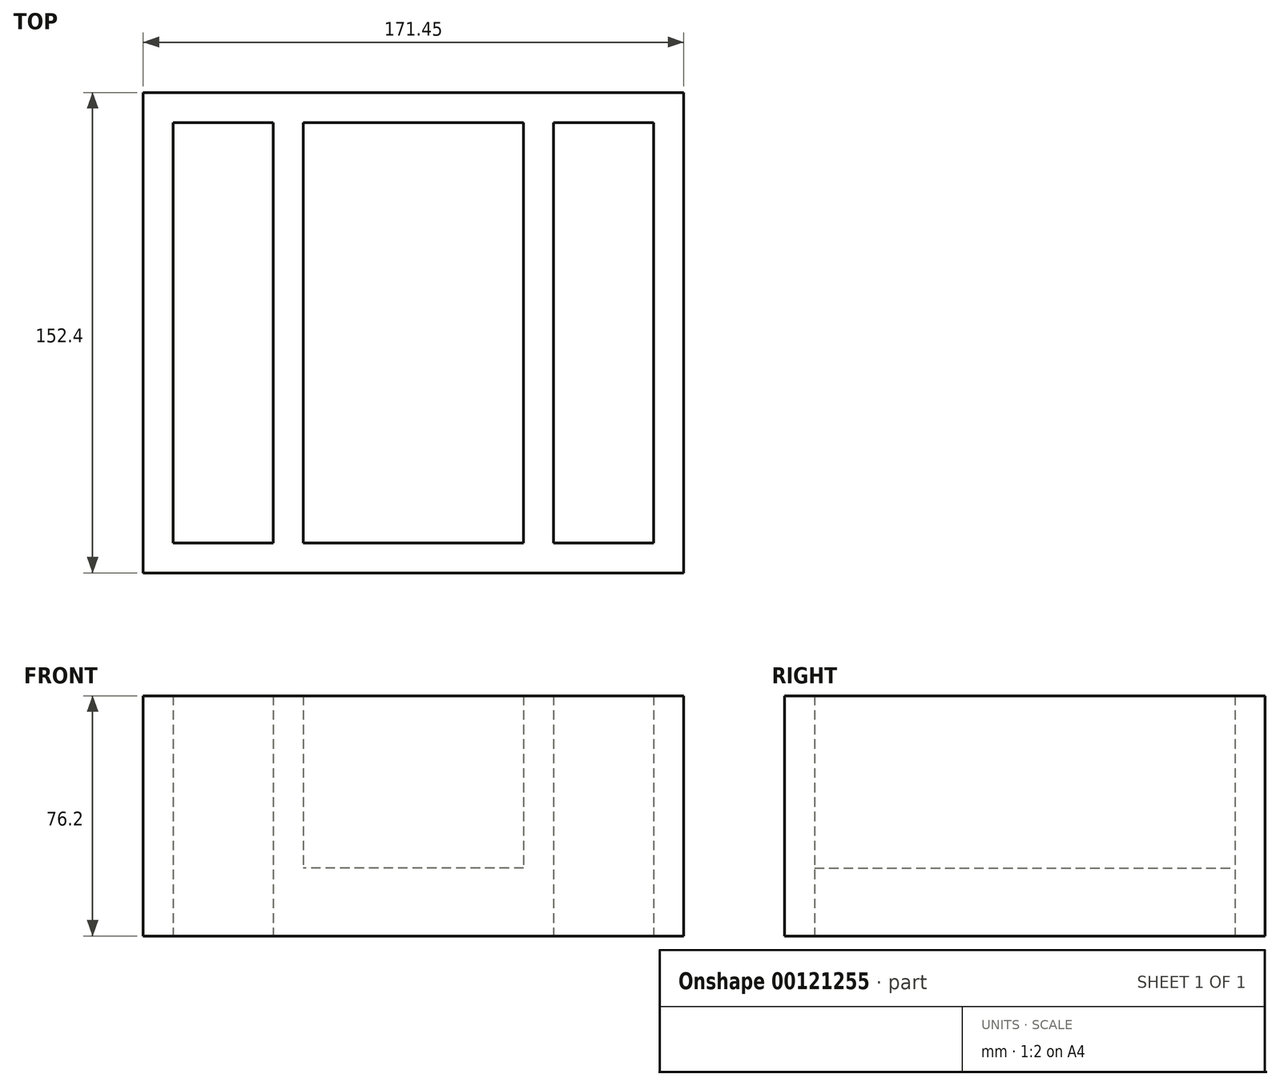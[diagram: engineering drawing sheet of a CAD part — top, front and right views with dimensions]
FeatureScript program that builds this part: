
annotation { "Feature Type Name" : "Feature", "Feature Type Description" : "" }
export const myFeature = defineFeature(function(context is Context, id is Id, definition is map)
    precondition{}
    {
        {
            var Q0;
            Q0=qCreatedBy(makeId("Top.planeOp"),FACE);
            var sketch = newSketch(context, id + "F0", { "sketchPlane" : qUnion([Q0])});
            skLineSegment(sketch, "E0.bottom", {"start": v(-137.66, 13.98) * mm, "end": v(33.79, 13.98) * mm});
            skLineSegment(sketch, "E0.top", {"start": v(-137.66, -138.42) * mm, "end": v(33.79, -138.42) * mm});
            skLineSegment(sketch, "E0.left", {"start": v(-137.66, 13.98) * mm, "end": v(-137.66, -138.42) * mm});
            skLineSegment(sketch, "E0.right", {"start": v(33.79, 13.98) * mm, "end": v(33.79, -138.42) * mm});
            skLineSegment(sketch, "E1.bottom", {"start": v(-128.14, 4.46) * mm, "end": v(-96.39, 4.46) * mm});
            skLineSegment(sketch, "E1.top", {"start": v(-128.14, -128.9) * mm, "end": v(-96.39, -128.9) * mm});
            skLineSegment(sketch, "E1.left", {"start": v(-128.14, 4.46) * mm, "end": v(-128.14, -128.9) * mm});
            skLineSegment(sketch, "E1.right", {"start": v(-96.39, 4.46) * mm, "end": v(-96.39, -128.9) * mm});
            skLineSegment(sketch, "E2.bottom", {"start": v(-7.49, 4.46) * mm, "end": v(24.26, 4.46) * mm});
            skLineSegment(sketch, "E2.top", {"start": v(-7.49, -128.9) * mm, "end": v(24.26, -128.9) * mm});
            skLineSegment(sketch, "E2.left", {"start": v(-7.49, 4.46) * mm, "end": v(-7.49, -128.9) * mm});
            skLineSegment(sketch, "E2.right", {"start": v(24.26, 4.46) * mm, "end": v(24.26, -128.9) * mm});
            skLineSegment(sketch, "E3", {"start": v(-96.39, 13.98) * mm, "end": v(-96.39, -138.42) * mm});
            skLineSegment(sketch, "E4", {"start": v(-7.49, 13.98) * mm, "end": v(-7.49, -138.42) * mm});
            skLineSegment(sketch, "E5.bottom", {"start": v(-86.86, 4.46) * mm, "end": v(-17.01, 4.46) * mm});
            skLineSegment(sketch, "E5.top", {"start": v(-86.86, -128.9) * mm, "end": v(-17.01, -128.9) * mm});
            skLineSegment(sketch, "E5.left", {"start": v(-86.86, 4.46) * mm, "end": v(-86.86, -128.9) * mm});
            skLineSegment(sketch, "E5.right", {"start": v(-17.01, 4.46) * mm, "end": v(-17.01, -128.9) * mm});
            skSolve(sketch);
        }
        {
            var Q0;
            {var subQ1=sQuery(id+"F0.wireOp",EDGE,"E0.left");Q0=makeQuery(id+"F0.imprint","IMPRINT",FACE,{"disambiguationData":[TD([[makeQuery(id+"F0.imprint","IMPRINT",EDGE,{"derivedFrom":subQ1}),1.0]])]});}
            var Q1;
            {var subQ1=sQuery(id+"F0.wireOp",EDGE,"E0.right");Q1=makeQuery(id+"F0.imprint","IMPRINT",FACE,{"disambiguationData":[TD([[makeQuery(id+"F0.imprint","IMPRINT",EDGE,{"derivedFrom":subQ1}),-1.0]])]});}
            var Q2;
            Q2=makeQuery(id+"F0.imprint","IMPRINT",FACE,{"disambiguationData":[TD([[makeQuery(id+"F0.imprint","IMPRINT",EDGE,{"derivedFrom":sQuery(id+"F0.wireOp",EDGE,"E5.bottom")}),1.0]])]});
            extrude(context, id + "F1", {"entities" : qUnion([Q0, Q1, Q2]), "depth" : 76.2 * mm});
        }
        {
            var Q0;
            Q0=makeQuery(id+"F1.opExtrude","SWEPT_FACE",FACE,{"disambiguationData":[OSD([sQuery(id+"F0.wireOp",EDGE,"E5.bottom")])]});
            var sketch = newSketch(context, id + "F2", { "sketchPlane" : qUnion([Q0])});
            skLineSegment(sketch, "E6", {"start": v(-17.01, 21.6) * mm, "end": v(-86.86, 21.59) * mm});
            skSolve(sketch);
        }
        {
            var Q0;
            Q0 = qSketchRegion(id + "F2", true);
            var Q1;
            {var subQ0=sQuery(id+"F2.wireOp",EDGE,"E6");Q1=makeQuery(id+"F2.imprint","IMPRINT",FACE,{"disambiguationData":[TD([[makeQuery(id+"F2.imprint","IMPRINT",EDGE,{"derivedFrom":subQ0}),1.0]])]});}
            extrude(context, id + "F3", {"entities" : qUnion([Q0, Q1]), "operationType" : NewBodyOperationType.ADD, "endBound" : BoundingType.UP_TO_NEXT, "depth" : 59.14 * mm});
        }
    });
